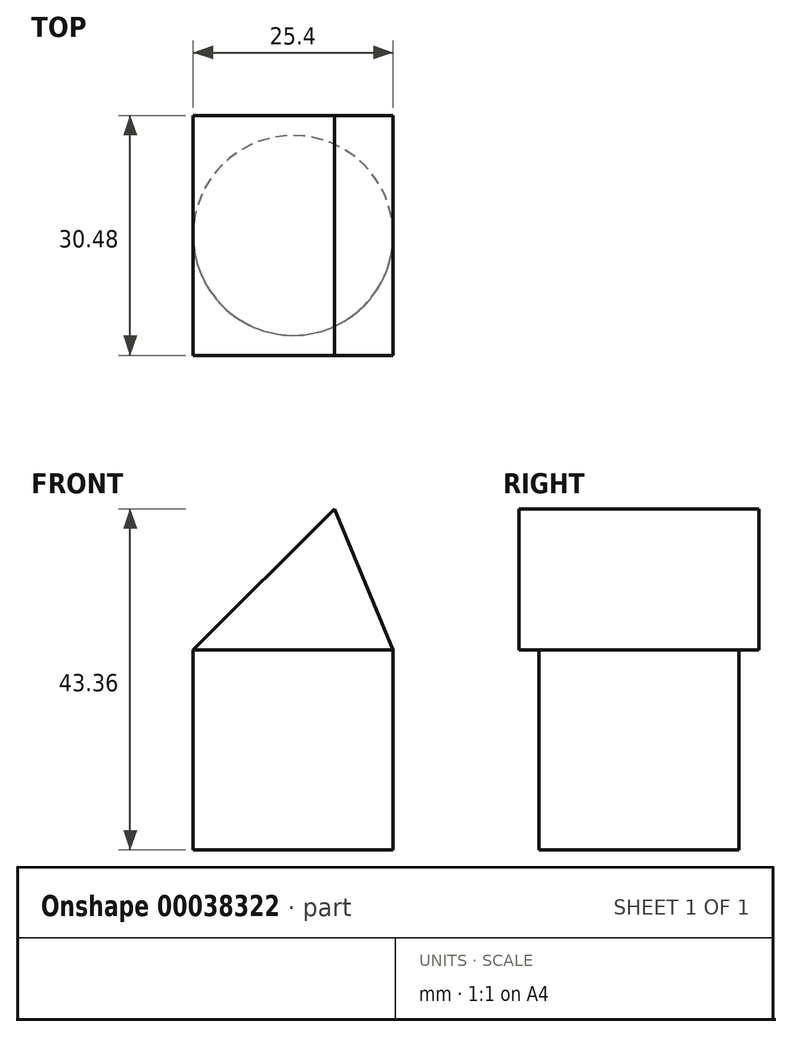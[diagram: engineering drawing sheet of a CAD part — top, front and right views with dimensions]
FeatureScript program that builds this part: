
annotation { "Feature Type Name" : "Feature", "Feature Type Description" : "" }
export const myFeature = defineFeature(function(context is Context, id is Id, definition is map)
    precondition{}
    {
        {
            var Q0;
            Q0=qCreatedBy(makeId("Front.planeOp"),FACE);
            var sketch = newSketch(context, id + "F0", { "sketchPlane" : qUnion([Q0])});
            skLineSegment(sketch, "E0.bottom", {"start": v(0, 0) * mm, "end": v(-25.4, 0) * mm});
            skLineSegment(sketch, "E0.top", {"start": v(0, -25.4) * mm, "end": v(-25.4, -25.4) * mm});
            skLineSegment(sketch, "E0.left", {"start": v(0, 0) * mm, "end": v(0, -25.4) * mm});
            skLineSegment(sketch, "E0.right", {"start": v(-25.4, 0) * mm, "end": v(-25.4, -25.4) * mm});
            skLineSegment(sketch, "E1.left", {"start": v(0, 0) * mm, "end": v(-7.44, 17.96) * mm});
            skLineSegment(sketch, "E2", {"start": v(-25.4, 0) * mm, "end": v(-7.44, 17.96) * mm});
            skLineSegment(sketch, "E3", {"start": v(-25.4, 0) * mm, "end": v(-43.36, 17.96) * mm});
            skLineSegment(sketch, "E4", {"start": v(-7.44, 17.96) * mm, "end": v(-25.4, 35.92) * mm});
            skLineSegment(sketch, "E5", {"start": v(-25.4, 35.92) * mm, "end": v(-43.36, 17.96) * mm});
            skSolve(sketch);
        }
        {
            var Q0;
            Q0 = qSketchRegion(id + "F0", true);
            extrude(context, id + "F1", {"entities" : qUnion([Q0]), "depth" : 30.48 * mm});
        }
        {
            var Q0;
            Q0=makeQuery(id+"F1.opExtrude","SWEPT_FACE",FACE,{"disambiguationData":[OSD([sQuery(id+"F0.wireOp",EDGE,"E0.top")])]});
            var sketch = newSketch(context, id + "F2", { "sketchPlane" : qUnion([Q0])});
            skCircle(sketch, "E6", {"center": v(-12.7, 15.24) * mm, "radius": 12.7 * mm});
            skPoint(sketch, "E6.centerSnap0", {"position": v(0, 15.24) * mm});
            skPoint(sketch, "E6.centerSnap1", {"position": v(-12.7, 30.48) * mm});
            skSolve(sketch);
        }
        {
            var Q0;
            {var subQ0=sQuery(id+"F0.wireOp",EDGE,"E0.top");var subQ4=makeQuery(id+"F1.opExtrude","CAP_EDGE",EDGE,{"disambiguationData":[OSD([subQ0])],"isStart":false});Q0=makeQuery(id+"F2.imprint","IMPRINT",FACE,{"disambiguationData":[TD([[makeQuery(id+"F2.imprint","IMPRINT",EDGE,{"derivedFrom":subQ4}),1.0]])]});}
            var Q1;
            {var subQ0=sQuery(id+"F0.wireOp",EDGE,"E0.top");var subQ4=makeQuery(id+"F1.opExtrude","CAP_EDGE",EDGE,{"disambiguationData":[OSD([subQ0])],"isStart":true});Q1=makeQuery(id+"F2.imprint","IMPRINT",FACE,{"disambiguationData":[TD([[makeQuery(id+"F2.imprint","IMPRINT",EDGE,{"derivedFrom":subQ4}),-1.0]])]});}
            extrude(context, id + "F3", {"entities" : qUnion([Q0, Q1]), "operationType" : NewBodyOperationType.REMOVE, "oppositeDirection" : true, "depth" : 25.4 * mm});
        }
        {
            var Q0;
            Q0=makeQuery(id+"F1.opExtrude","SWEPT_FACE",FACE,{"disambiguationData":[OSD([sQuery(id+"F0.wireOp",EDGE,"E5")])]});
            var sketch = newSketch(context, id + "F4", { "sketchPlane" : qUnion([Q0])});
            skCircle(sketch, "E7", {"center": v(-5.26, -15.24) * mm, "radius": 12.7 * mm});
            skPoint(sketch, "E7.centerSnap0", {"position": v(-5.26, -30.48) * mm});
            skPoint(sketch, "E7.centerSnap1", {"position": v(7.44, -15.24) * mm});
            skSolve(sketch);
        }
        {
            var Q0;
            {var subQ0=sQuery(id+"F0.wireOp",EDGE,"E5");var subQ4=makeQuery(id+"F1.opExtrude","CAP_EDGE",EDGE,{"disambiguationData":[OSD([subQ0])],"isStart":true});Q0=makeQuery(id+"F4.imprint","IMPRINT",FACE,{"disambiguationData":[TD([[makeQuery(id+"F4.imprint","IMPRINT",EDGE,{"derivedFrom":subQ4}),1.0]])]});}
            var Q1;
            {var subQ0=sQuery(id+"F0.wireOp",EDGE,"E5");var subQ4=makeQuery(id+"F1.opExtrude","CAP_EDGE",EDGE,{"disambiguationData":[OSD([subQ0])],"isStart":false});Q1=makeQuery(id+"F4.imprint","IMPRINT",FACE,{"disambiguationData":[TD([[makeQuery(id+"F4.imprint","IMPRINT",EDGE,{"derivedFrom":subQ4}),-1.0]])]});}
            extrude(context, id + "F5", {"entities" : qUnion([Q0, Q1]), "operationType" : NewBodyOperationType.REMOVE, "oppositeDirection" : true, "depth" : 25.4 * mm});
        }
    });
